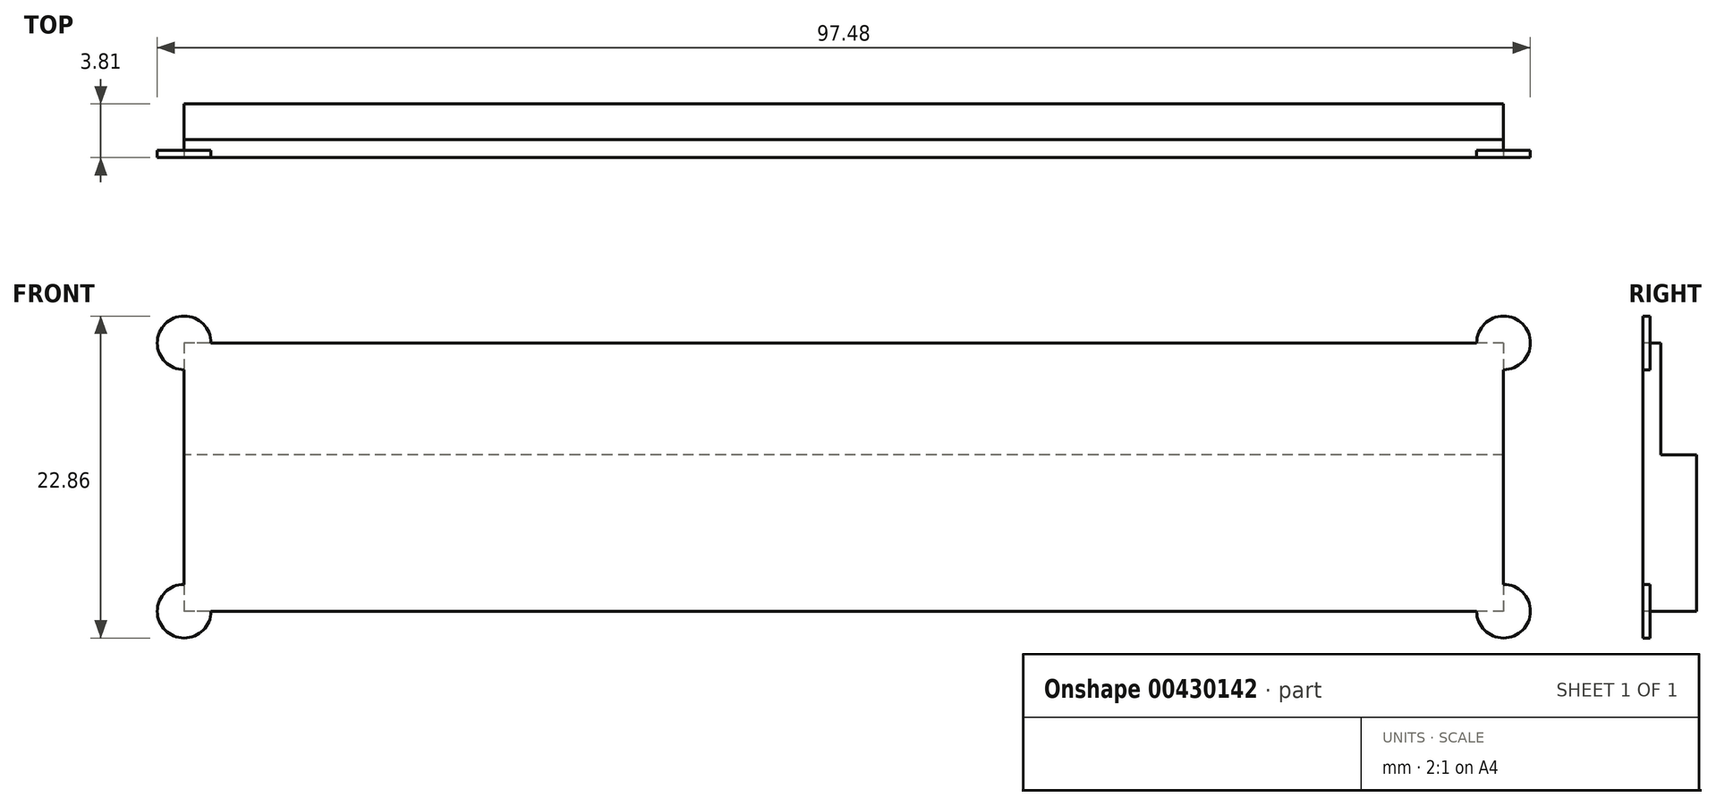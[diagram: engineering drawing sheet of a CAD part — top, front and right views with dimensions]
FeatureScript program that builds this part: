
annotation { "Feature Type Name" : "Feature", "Feature Type Description" : "" }
export const myFeature = defineFeature(function(context is Context, id is Id, definition is map)
    precondition{}
    {
        {
            var Q0;
            Q0=qCreatedBy(makeId("Right.planeOp"),FACE);
            var sketch = newSketch(context, id + "F0", { "sketchPlane" : qUnion([Q0])});
            skLineSegment(sketch, "E0.bottom", {"start": v(2.54, 9.52) * mm, "end": v(1.27, 9.52) * mm});
            skLineSegment(sketch, "E0.top", {"start": v(2.54, -9.52) * mm, "end": v(-2.54, -9.52) * mm});
            skLineSegment(sketch, "E0.left", {"start": v(2.54, 9.53) * mm, "end": v(2.54, -9.52) * mm});
            skLineSegment(sketch, "E0.right", {"start": v(-2.54, 9.52) * mm, "end": v(-2.54, -9.52) * mm});
            skPoint(sketch, "E0.middle", {"position": v(0, 0) * mm});
            skLineSegment(sketch, "E1", {"start": v(-1.27, 9.52) * mm, "end": v(-1.27, 1.59) * mm});
            skLineSegment(sketch, "E2", {"start": v(-1.27, 1.59) * mm, "end": v(1.27, 1.59) * mm});
            skLineSegment(sketch, "E3", {"start": v(1.27, 1.59) * mm, "end": v(1.27, 9.53) * mm});
            skLineSegment(sketch, "E4.trimOffspring", {"start": v(-1.27, 9.52) * mm, "end": v(-2.54, 9.52) * mm});
            skLineSegment(sketch, "E5", {"start": v(1.27, 1.59) * mm, "end": v(1.27, -9.52) * mm});
            skSolve(sketch);
        }
        {
            var Q0;
            {var subQ0=sQuery(id+"F0.wireOp",EDGE,"E0.right");Q0=makeQuery(id+"F0.imprint","IMPRINT",FACE,{"disambiguationData":[TD([[makeQuery(id+"F0.imprint","IMPRINT",EDGE,{"derivedFrom":subQ0}),1.0]])]});}
            extrude(context, id + "F1", {"entities" : qUnion([Q0]), "depth" : 93.66 * mm});
        }
        {
            var Q0;
            Q0=makeQuery(id+"F1.opExtrude","SWEPT_FACE",FACE,{"disambiguationData":[OSD([sQuery(id+"F0.wireOp",EDGE,"E0.right")])]});
            var sketch = newSketch(context, id + "F2", { "sketchPlane" : qUnion([Q0])});
            skCircle(sketch, "E6", {"center": v(93.66, -9.52) * mm, "radius": 1.9 * mm});
            skCircle(sketch, "E7", {"center": v(93.66, 9.52) * mm, "radius": 1.9 * mm});
            skCircle(sketch, "E8", {"center": v(0, -9.52) * mm, "radius": 1.9 * mm});
            skCircle(sketch, "E9", {"center": v(0, 9.52) * mm, "radius": 1.9 * mm});
            skSolve(sketch);
        }
        {
            var Q0;
            {var subQ0=sQuery(id+"F2.wireOp",EDGE,"E7");var subQ1=sQuery(id+"F0.wireOp",EDGE,"E0.right");var subQ4=makeQuery(id+"F1.opExtrude","CAP_EDGE",EDGE,{"disambiguationData":[OSD([subQ1])],"isStart":false});var subQ5=makeQuery(id+"F2.imprint","INTERSECT",VERTEX,{"derivedFrom":[subQ4,subQ0]});Q0=makeQuery(id+"F2.imprint","IMPRINT",FACE,{"disambiguationData":[TD([[makeQuery(id+"F2.imprint","IMPRINT",EDGE,{"disambiguationData":[TD([[subQ5,-1.0]])],"derivedFrom":subQ0}),1.0]])]});}
            var Q1;
            {var subQ0=sQuery(id+"F2.wireOp",EDGE,"E6");var subQ1=sQuery(id+"F0.wireOp",EDGE,"E0.right");var subQ4=makeQuery(id+"F1.opExtrude","CAP_EDGE",EDGE,{"disambiguationData":[OSD([subQ1])],"isStart":false});var subQ5=makeQuery(id+"F2.imprint","INTERSECT",VERTEX,{"derivedFrom":[subQ4,subQ0]});Q1=makeQuery(id+"F2.imprint","IMPRINT",FACE,{"disambiguationData":[TD([[makeQuery(id+"F2.imprint","IMPRINT",EDGE,{"disambiguationData":[TD([[subQ5,1.0]])],"derivedFrom":subQ0}),1.0]])]});}
            var Q2;
            {var subQ0=sQuery(id+"F2.wireOp",EDGE,"E8");var subQ1=sQuery(id+"F0.wireOp",EDGE,"E0.right");var subQ4=makeQuery(id+"F1.opExtrude","CAP_EDGE",EDGE,{"disambiguationData":[OSD([subQ1])],"isStart":true});var subQ5=makeQuery(id+"F2.imprint","INTERSECT",VERTEX,{"derivedFrom":[subQ4,subQ0]});Q2=makeQuery(id+"F2.imprint","IMPRINT",FACE,{"disambiguationData":[TD([[makeQuery(id+"F2.imprint","IMPRINT",EDGE,{"disambiguationData":[TD([[subQ5,-1.0]])],"derivedFrom":subQ0}),1.0]])]});}
            var Q3;
            {var subQ0=sQuery(id+"F2.wireOp",EDGE,"E9");var subQ1=sQuery(id+"F0.wireOp",EDGE,"E0.right");var subQ4=makeQuery(id+"F1.opExtrude","CAP_EDGE",EDGE,{"disambiguationData":[OSD([subQ1])],"isStart":true});var subQ5=makeQuery(id+"F2.imprint","INTERSECT",VERTEX,{"derivedFrom":[subQ4,subQ0]});Q3=makeQuery(id+"F2.imprint","IMPRINT",FACE,{"disambiguationData":[TD([[makeQuery(id+"F2.imprint","IMPRINT",EDGE,{"disambiguationData":[TD([[subQ5,1.0]])],"derivedFrom":subQ0}),1.0]])]});}
            var Q4;
            Q4 = qConstructionFilter(qBodyType(qCreatedBy(id + "F2" ,EDGE), BodyType.WIRE), ConstructionObject.NO);
            extrude(context, id + "F3", {"entities" : qUnion([Q0, Q1, Q2, Q3]), "operationType" : NewBodyOperationType.ADD, "surfaceEntities" : qUnion([Q4]), "oppositeDirection" : true, "depth" : 0.5 * mm});
        }
    });
